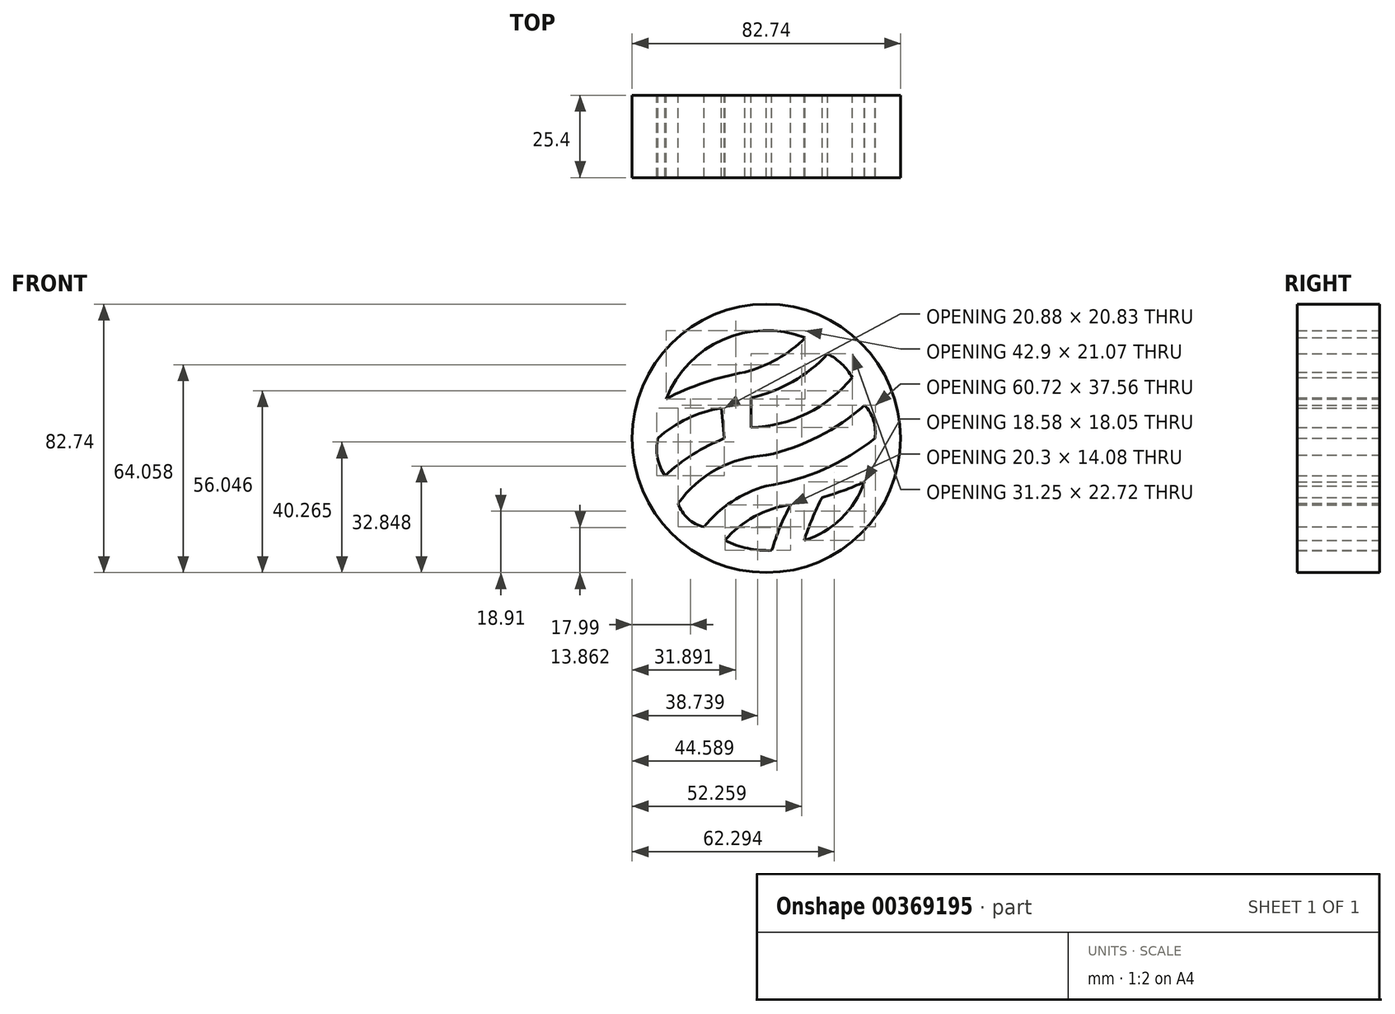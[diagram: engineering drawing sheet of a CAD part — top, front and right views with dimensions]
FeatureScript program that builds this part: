
annotation { "Feature Type Name" : "Feature", "Feature Type Description" : "" }
export const myFeature = defineFeature(function(context is Context, id is Id, definition is map)
    precondition{}
    {
        {
            var Q0;
            Q0=qCreatedBy(makeId("Front.planeOp"),FACE);
            var sketch = newSketch(context, id + "F0", { "sketchPlane" : qUnion([Q0])});
            skCircle(sketch, "E0", {"center": v(0, 0) * mm, "radius": 41.37 * mm});
            skArc(sketch, "E1", {"start": v(-30.93, 12.15) * mm, "mid": v(-13.37, 30.43) * mm, "end": v(11.97, 31) * mm});
            skArc(sketch, "E2", {"start": v(-6.63, 20.36) * mm, "mid": v(-19.1, 17.2) * mm, "end": v(-30.93, 12.15) * mm});
            skArc(sketch, "E3", {"start": v(-13.89, 9.31) * mm, "mid": v(-24.35, 6.08) * mm, "end": v(-33.46, 0) * mm});
            skArc(sketch, "E4", {"start": v(-12.94, 0) * mm, "mid": v(-22.63, -4.91) * mm, "end": v(-31.25, -11.52) * mm});
            skArc(sketch, "E5", {"start": v(-33.46, 0) * mm, "mid": v(-33.56, -6) * mm, "end": v(-31.25, -11.52) * mm});
            skLineSegment(sketch, "E6", {"start": v(-13.89, 9.31) * mm, "end": v(-12.94, 0) * mm});
            skArc(sketch, "E7", {"start": v(-6.63, 20.36) * mm, "mid": v(3.37, 24.46) * mm, "end": v(11.97, 31) * mm});
            skArc(sketch, "E8", {"start": v(-4.73, 12.47) * mm, "mid": v(8.12, 17.47) * mm, "end": v(18.94, 26.04) * mm});
            skArc(sketch, "E9", {"start": v(-4.73, 3.31) * mm, "mid": v(12.56, 7.67) * mm, "end": v(26.51, 18.78) * mm});
            skLineSegment(sketch, "E10", {"start": v(-4.73, 3.31) * mm, "end": v(-4.73, 12.47) * mm});
            skArc(sketch, "E11", {"start": v(26.51, 18.78) * mm, "mid": v(23.23, 22.94) * mm, "end": v(18.94, 26.04) * mm});
            skArc(sketch, "E12", {"start": v(0, -5.2) * mm, "mid": v(-15.27, -9.52) * mm, "end": v(-27.14, -20.04) * mm});
            skArc(sketch, "E13", {"start": v(0, -5.2) * mm, "mid": v(16.16, 0.56) * mm, "end": v(30.3, 10.26) * mm});
            skArc(sketch, "E14", {"start": v(33.46, 0) * mm, "mid": v(33.04, 5.49) * mm, "end": v(30.3, 10.26) * mm});
            skArc(sketch, "E15", {"start": v(0, -14.68) * mm, "mid": v(17.7, -9.54) * mm, "end": v(33.46, 0) * mm});
            skArc(sketch, "E16", {"start": v(0, -14.68) * mm, "mid": v(-10.61, -19.48) * mm, "end": v(-19.25, -27.3) * mm});
            skArc(sketch, "E17", {"start": v(-27.14, -20.04) * mm, "mid": v(-24.18, -24.75) * mm, "end": v(-19.25, -27.3) * mm});
            skArc(sketch, "E18", {"start": v(7.52, -20.47) * mm, "mid": v(4.2, -27.34) * mm, "end": v(1.68, -34.54) * mm});
            skArc(sketch, "E19", {"start": v(-12.78, -31.48) * mm, "mid": v(-5.74, -33.9) * mm, "end": v(1.68, -34.54) * mm});
            skArc(sketch, "E20", {"start": v(7.52, -20.47) * mm, "mid": v(-3.66, -24.08) * mm, "end": v(-12.78, -31.48) * mm});
            skArc(sketch, "E21", {"start": v(17.2, -18.21) * mm, "mid": v(23.8, -16.06) * mm, "end": v(30.21, -13.44) * mm});
            skArc(sketch, "E22", {"start": v(11.63, -31.48) * mm, "mid": v(23.1, -24.69) * mm, "end": v(30.21, -13.44) * mm});
            skArc(sketch, "E23", {"start": v(17.2, -18.21) * mm, "mid": v(14.15, -24.73) * mm, "end": v(11.63, -31.48) * mm});
            skSolve(sketch);
        }
        {
            var Q0;
            Q0 = qSketchRegion(id + "F0", true);
            extrude(context, id + "F1", {"entities" : qUnion([Q0]), "depth" : 25.4 * mm});
        }
    });
